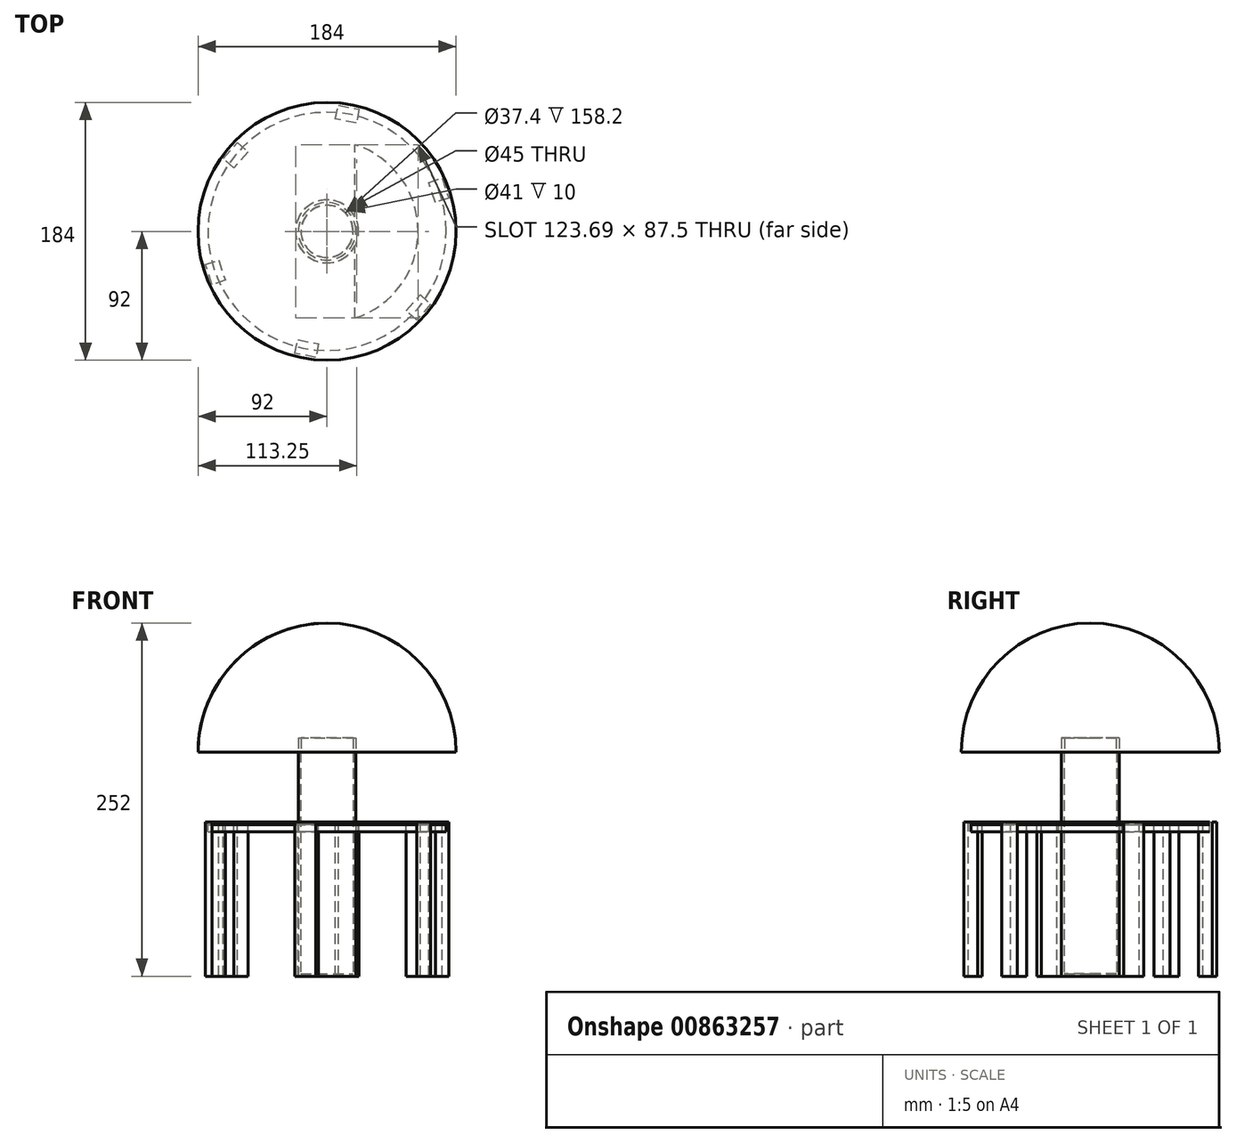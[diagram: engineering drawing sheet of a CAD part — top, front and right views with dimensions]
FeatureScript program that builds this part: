
annotation { "Feature Type Name" : "Feature", "Feature Type Description" : "" }
export const myFeature = defineFeature(function(context is Context, id is Id, definition is map)
    precondition{}
    {
        {
            var Q0;
            Q0=qCreatedBy(makeId("Top.planeOp"),FACE);
            var sketch = newSketch(context, id + "F0", { "sketchPlane" : qUnion([Q0])});
            skCircle(sketch, "E0", {"center": v(0, 0) * mm, "radius": 85 * mm});
            skLineSegment(sketch, "E1", {"start": v(0, 0) * mm, "end": v(15, 0) * mm, "construction": true});
            skLineSegment(sketch, "E2", {"start": v(0, 0) * mm, "end": v(-15, 0) * mm, "construction": true});
            skLineSegment(sketch, "E3", {"start": v(0, 0) * mm, "end": v(0, -65) * mm, "construction": true});
            skLineSegment(sketch, "E4", {"start": v(0, 0) * mm, "end": v(0, 65) * mm, "construction": true});
            skLineSegment(sketch, "E5", {"start": v(0, 65) * mm, "end": v(15, 65) * mm, "construction": true});
            skLineSegment(sketch, "E6", {"start": v(0, 65) * mm, "end": v(-15, 65) * mm, "construction": true});
            skCircle(sketch, "E7", {"center": v(0, 0) * mm, "radius": 65 * mm});
            skLineSegment(sketch, "E8.bottom", {"start": v(20, -93.84) * mm, "end": v(-20, -93.84) * mm});
            skLineSegment(sketch, "E8.top", {"start": v(20, 93.84) * mm, "end": v(-20, 93.84) * mm});
            skLineSegment(sketch, "E8.left", {"start": v(20, -93.84) * mm, "end": v(20, 93.84) * mm});
            skLineSegment(sketch, "E8.right", {"start": v(-20, -93.84) * mm, "end": v(-20, 93.84) * mm});
            skSolve(sketch);
        }
        {
            var Q0;
            Q0=qCreatedBy(makeId("Top.planeOp"),FACE);
            var sketch = newSketch(context, id + "F1", { "sketchPlane" : qUnion([Q0])});
            skCircle(sketch, "E9.0", {"center": v(0, 0) * mm, "radius": 85 * mm});
            skSolve(sketch);
        }
        {
            var Q0;
            Q0=makeQuery(id+"F1.imprint","IMPRINT",FACE,{"disambiguationData":[TD([[makeQuery(id+"F1.imprint","IMPRINT",EDGE,{"derivedFrom":sQuery(id+"F1.wireOp",EDGE,"E9.0")}),1.0]])]});
            extrude(context, id + "F2", {"entities" : qUnion([Q0]), "oppositeDirection" : true, "depth" : 7 * mm, "offsetDistance" : 25 * mm});
        }
        {
            var Q0;
            {var subQ0=sQuery(id+"F0.wireOp",EDGE,"E8.right");var subQ1=sQuery(id+"F0.wireOp",EDGE,"E0");var subQ2=makeQuery(id+"F0.imprint","INTERSECT",VERTEX,{"disambiguationData":[OD(0.0)],"derivedFrom":[subQ1,subQ0]});Q0=makeQuery(id+"F0.imprint","IMPRINT",FACE,{"disambiguationData":[TD([[makeQuery(id+"F0.imprint","IMPRINT",EDGE,{"disambiguationData":[TD([[subQ2,-1.0]])],"derivedFrom":subQ1}),1.0]])]});}
            var Q1;
            {var subQ0=sQuery(id+"F0.wireOp",EDGE,"E8.right");var subQ1=sQuery(id+"F0.wireOp",EDGE,"E0");var subQ2=makeQuery(id+"F0.imprint","INTERSECT",VERTEX,{"disambiguationData":[OD(0.0)],"derivedFrom":[subQ1,subQ0]});Q1=makeQuery(id+"F0.imprint","IMPRINT",FACE,{"disambiguationData":[TD([[makeQuery(id+"F0.imprint","IMPRINT",EDGE,{"disambiguationData":[TD([[subQ2,1.0]])],"derivedFrom":subQ1}),1.0]])]});}
            var Q2;
            {var subQ0=sQuery(id+"F0.wireOp",EDGE,"E8.left");var subQ1=sQuery(id+"F0.wireOp",EDGE,"E0");var subQ2=makeQuery(id+"F0.imprint","INTERSECT",VERTEX,{"disambiguationData":[OD(0.0)],"derivedFrom":[subQ1,subQ0]});Q2=makeQuery(id+"F0.imprint","IMPRINT",FACE,{"disambiguationData":[TD([[makeQuery(id+"F0.imprint","IMPRINT",EDGE,{"disambiguationData":[TD([[subQ2,1.0]])],"derivedFrom":subQ1}),1.0]])]});}
            var Q3;
            {var subQ0=sQuery(id+"F0.wireOp",EDGE,"E8.right");var subQ1=sQuery(id+"F0.wireOp",EDGE,"E0");var subQ2=makeQuery(id+"F0.imprint","INTERSECT",VERTEX,{"disambiguationData":[OD(1.0)],"derivedFrom":[subQ1,subQ0]});Q3=makeQuery(id+"F0.imprint","IMPRINT",FACE,{"disambiguationData":[TD([[makeQuery(id+"F0.imprint","IMPRINT",EDGE,{"disambiguationData":[TD([[subQ2,-1.0]])],"derivedFrom":subQ1}),1.0]])]});}
            var Q4;
            {var subQ0=sQuery(id+"F0.wireOp",EDGE,"E8.left");var subQ1=sQuery(id+"F0.wireOp",EDGE,"E7");var subQ2=makeQuery(id+"F0.imprint","INTERSECT",VERTEX,{"disambiguationData":[OD(0.0)],"derivedFrom":[subQ1,subQ0]});Q4=makeQuery(id+"F0.imprint","IMPRINT",FACE,{"disambiguationData":[TD([[makeQuery(id+"F0.imprint","IMPRINT",EDGE,{"disambiguationData":[TD([[subQ2,1.0]])],"derivedFrom":subQ1}),1.0]])]});}
            var Q5;
            {var subQ0=sQuery(id+"F0.wireOp",EDGE,"E8.right");var subQ1=sQuery(id+"F0.wireOp",EDGE,"E7");var subQ2=makeQuery(id+"F0.imprint","INTERSECT",VERTEX,{"disambiguationData":[OD(0.0)],"derivedFrom":[subQ1,subQ0]});Q5=makeQuery(id+"F0.imprint","IMPRINT",FACE,{"disambiguationData":[TD([[makeQuery(id+"F0.imprint","IMPRINT",EDGE,{"disambiguationData":[TD([[subQ2,-1.0]])],"derivedFrom":subQ1}),1.0]])]});}
            var Q6;
            {var subQ0=sQuery(id+"F0.wireOp",EDGE,"E8.right");var subQ1=sQuery(id+"F0.wireOp",EDGE,"E7");var subQ2=makeQuery(id+"F0.imprint","INTERSECT",VERTEX,{"disambiguationData":[OD(0.0)],"derivedFrom":[subQ1,subQ0]});Q6=makeQuery(id+"F0.imprint","IMPRINT",FACE,{"disambiguationData":[TD([[makeQuery(id+"F0.imprint","IMPRINT",EDGE,{"disambiguationData":[TD([[subQ2,1.0]])],"derivedFrom":subQ1}),1.0]])]});}
            extrude(context, id + "F3", {"entities" : qUnion([Q0, Q1, Q2, Q3, Q4, Q5, Q6]), "oppositeDirection" : true, "depth" : 1.8 * mm, "offsetDistance" : 25 * mm});
        }
        {
            var Q0;
            {var subQ0=sQuery(id+"F0.wireOp",EDGE,"E0");Q0=makeQuery(id+"F92N3ToIArTKFft_1.boolean.opBoolean","SPLIT",FACE,{"disambiguationData":[TD([makeQuery(id+"FFIeb2ztRoP1rm2_1.boolean.opBoolean","COPY",FACE,{"derivedFrom":makeQuery(id+"FFIeb2ztRoP1rm2_1.opExtrude","SWEPT_FACE",FACE,{"disambiguationData":[OSD([sQuery(id+"FUWerJDIJFKlQu6_1.wireOp",EDGE,"KzpTdK0h-yw9V-XJjy-UJbk-oXAReHN1zFgU.left")])]})})])],"derivedFrom":makeQuery(id+"F3.opExtrude","CAP_FACE",FACE,{"disambiguationData":[OSD([subQ0])],"isStart":true})});}
            var sketch = newSketch(context, id + "F4", { "sketchPlane" : qUnion([Q0])});
            skLineSegment(sketch, "E10", {"start": v(-25, 60) * mm, "end": v(-60.2, 60) * mm, "construction": true});
            skLineSegment(sketch, "E11", {"start": v(-60.2, 60) * mm, "end": v(-45.17, 46.74) * mm, "construction": true});
            skLineSegment(sketch, "E12", {"start": v(-60.2, 60) * mm, "end": v(-56.46, 56.7) * mm});
            skLineSegment(sketch, "E13", {"start": v(-56.46, 56.7) * mm, "end": v(-66.46, 45.34) * mm});
            skLineSegment(sketch, "E14", {"start": v(-66.46, 45.34) * mm, "end": v(-73.96, 51.96) * mm});
            skLineSegment(sketch, "E15", {"start": v(-73.96, 51.96) * mm, "end": v(-63.96, 63.3) * mm});
            skLineSegment(sketch, "E16", {"start": v(-63.96, 63.3) * mm, "end": v(-56.46, 56.7) * mm});
            skSolve(sketch);
        }
        {
            var Q0;
            {var subQ0=sQuery(id+"F4.wireOp",EDGE,"E15");Q0=makeQuery(id+"F4.imprint","IMPRINT",FACE,{"disambiguationData":[TD([[makeQuery(id+"F4.imprint","IMPRINT",EDGE,{"derivedFrom":subQ0}),-1.0]])]});}
            var Q1;
            {var subQ0=sQuery(id+"F4.wireOp",EDGE,"E13");Q1=makeQuery(id+"F4.imprint","IMPRINT",FACE,{"disambiguationData":[TD([[makeQuery(id+"F4.imprint","IMPRINT",EDGE,{"derivedFrom":subQ0}),-1.0]])]});}
            extrude(context, id + "F5", {"entities" : qUnion([Q0, Q1]), "oppositeDirection" : true, "depth" : 110 * mm, "offsetDistance" : 25 * mm});
        }
        {
            var Q0;
            Q0=qCreatedBy(makeId("Right.planeOp"),FACE);
            var sketch = newSketch(context, id + "F6", { "sketchPlane" : qUnion([Q0])});
            skLineSegment(sketch, "E17", {"start": v(0, 0) * mm, "end": v(0, 63.94) * mm, "construction": true});
            skSolve(sketch);
        }
        {
            var Q0;
            Q0=makeQuery(id+"F5.opExtrude","SWEPT_BODY",BODY,{"disambiguationData":[OSD([sQuery(id+"F4.wireOp",EDGE,"E13"),sQuery(id+"F4.wireOp",EDGE,"E14"),sQuery(id+"F4.wireOp",EDGE,"E15"),sQuery(id+"F4.wireOp",EDGE,"E16")])]});
            var Q1;
            Q1=sQuery(id+"F6.wireOp",EDGE,"E17");
            circularPattern(context, id + "F7", {"entities" : qUnion([Q0]), "axis" : qUnion([Q1]), "angle" : 360 * degree, "instanceCount" : 6, "equalSpace" : true});
        }
        {
            var Q0;
            Q0=makeQuery(id+"F5.opExtrude","CAP_FACE",FACE,{"disambiguationData":[OSD([sQuery(id+"F4.wireOp",EDGE,"E13"),sQuery(id+"F4.wireOp",EDGE,"E14"),sQuery(id+"F4.wireOp",EDGE,"E15"),sQuery(id+"F4.wireOp",EDGE,"E16")])],"isStart":false});
            var sketch = newSketch(context, id + "F8", { "sketchPlane" : qUnion([Q0])});
            skCircle(sketch, "E18", {"center": v(0, 0) * mm, "radius": 92 * mm});
            skSolve(sketch);
        }
        {
            var Q0;
            {var subQ0=sQuery(id+"F0.wireOp",EDGE,"E8.right");var subQ1=sQuery(id+"F0.wireOp",EDGE,"E7");var subQ2=makeQuery(id+"F0.imprint","INTERSECT",VERTEX,{"disambiguationData":[OD(0.0)],"derivedFrom":[subQ1,subQ0]});Q0=makeQuery(id+"F0.imprint","IMPRINT",FACE,{"disambiguationData":[TD([[makeQuery(id+"F0.imprint","IMPRINT",EDGE,{"disambiguationData":[TD([[subQ2,1.0]])],"derivedFrom":subQ1}),1.0]])]});}
            var sketch = newSketch(context, id + "F9", { "sketchPlane" : qUnion([Q0])});
            skCircle(sketch, "E19", {"center": v(0, 0) * mm, "radius": 22.5 * mm});
            skSolve(sketch);
        }
        {
            var Q0;
            Q0 = qSketchRegion(id + "F9", true);
            extrude(context, id + "F10", {"entities" : qUnion([Q0]), "operationType" : NewBodyOperationType.REMOVE, "oppositeDirection" : true, "depth" : 25 * mm, "offsetDistance" : 25 * mm});
        }
        {
            var Q0;
            Q0=makeQuery(id+"F8.imprint","IMPRINT",FACE,{"disambiguationData":[TD([[makeQuery(id+"F8.imprint","IMPRINT",EDGE,{"derivedFrom":sQuery(id+"F8.wireOp",EDGE,"E18")}),1.0]])]});
            var sketch = newSketch(context, id + "F11", { "sketchPlane" : qUnion([Q0])});
            skCircle(sketch, "E20.0", {"center": v(0, 0) * mm, "radius": 22.5 * mm});
            skCircle(sketch, "E21.0", {"center": v(0, 0) * mm, "radius": 20.5 * mm});
            skSolve(sketch);
        }
        {
            var Q0;
            Q0=makeQuery(id+"F11.imprint","IMPRINT",FACE,{"disambiguationData":[TD([[makeQuery(id+"F11.imprint","IMPRINT",EDGE,{"derivedFrom":sQuery(id+"F11.wireOp",EDGE,"E21.0")}),1.0]])]});
            extrude(context, id + "F12", {"entities" : qUnion([Q0]), "oppositeDirection" : true, "depth" : 160 * mm, "offsetDistance" : 25 * mm});
        }
        {
            var Q0;
            Q0=makeQuery(id+"F12.opExtrude","CAP_FACE",FACE,{"disambiguationData":[OSD([sQuery(id+"F11.wireOp",EDGE,"E21.0")])],"isStart":false});
            var sketch = newSketch(context, id + "F13", { "sketchPlane" : qUnion([Q0])});
            skCircle(sketch, "E22.0", {"center": v(0, 0) * mm, "radius": 20.5 * mm});
            skCircle(sketch, "E23.0", {"center": v(0, 0) * mm, "radius": 92 * mm});
            skSolve(sketch);
        }
        {
            var Q0;
            Q0=qCreatedBy(makeId("Front.planeOp"),FACE);
            var sketch = newSketch(context, id + "F14", { "sketchPlane" : qUnion([Q0])});
            skLineSegment(sketch, "E24.0", {"start": v(92, 50) * mm, "end": v(-92, 50) * mm});
            skArc(sketch, "E25", {"start": v(-92, 50) * mm, "mid": v(-65.05, 115.05) * mm, "end": v(0, 142) * mm});
            skLineSegment(sketch, "E26", {"start": v(0, 142) * mm, "end": v(0, 50) * mm});
            skSolve(sketch);
        }
        {
            var Q0;
            Q0 = qSketchRegion(id + "F14", true);
            var Q1;
            Q1=sQuery(id+"F14.wireOp",EDGE,"E26");
            revolve(context, id + "F15", {"surfaceOperationType" : NewSurfaceOperationType.NEW, "entities" : qUnion([Q0]), "axis" : qUnion([Q1]), "revolveType" : RevolveType.FULL});
        }
        {
            var Q0;
            Q0=makeQuery(id+"F13.imprint","IMPRINT",FACE,{"disambiguationData":[TD([[makeQuery(id+"F13.imprint","IMPRINT",EDGE,{"derivedFrom":sQuery(id+"F13.wireOp",EDGE,"E22.0")}),1.0]])]});
            var sketch = newSketch(context, id + "F16", { "sketchPlane" : qUnion([Q0])});
            skCircle(sketch, "E27.0", {"center": v(0, 0) * mm, "radius": 20.5 * mm});
            skCircle(sketch, "E28.0", {"center": v(0, 0) * mm, "radius": 18.5 * mm});
            skCircle(sketch, "E29.0", {"center": v(0, 0) * mm, "radius": 97 * mm});
            skSolve(sketch);
        }
        {
            var Q0;
            Q0=makeQuery(id+"F16.imprint","IMPRINT",FACE,{"disambiguationData":[TD([[makeQuery(id+"F16.imprint","IMPRINT",EDGE,{"derivedFrom":sQuery(id+"F16.wireOp",EDGE,"E28.0")}),-1.0]])]});
            extrude(context, id + "F17", {"entities" : qUnion([Q0]), "operationType" : NewBodyOperationType.REMOVE, "depth" : 10 * mm, "offsetDistance" : 25 * mm});
        }
        {
            var Q0;
            Q0=makeQuery(id+"F12.opExtrude","CAP_FACE",FACE,{"disambiguationData":[OSD([sQuery(id+"F11.wireOp",EDGE,"E21.0")])],"isStart":false});
            shell(context, id + "F18", {"entities" : qUnion([Q0]), "thickness" : 1.8 * mm});
        }
    });
